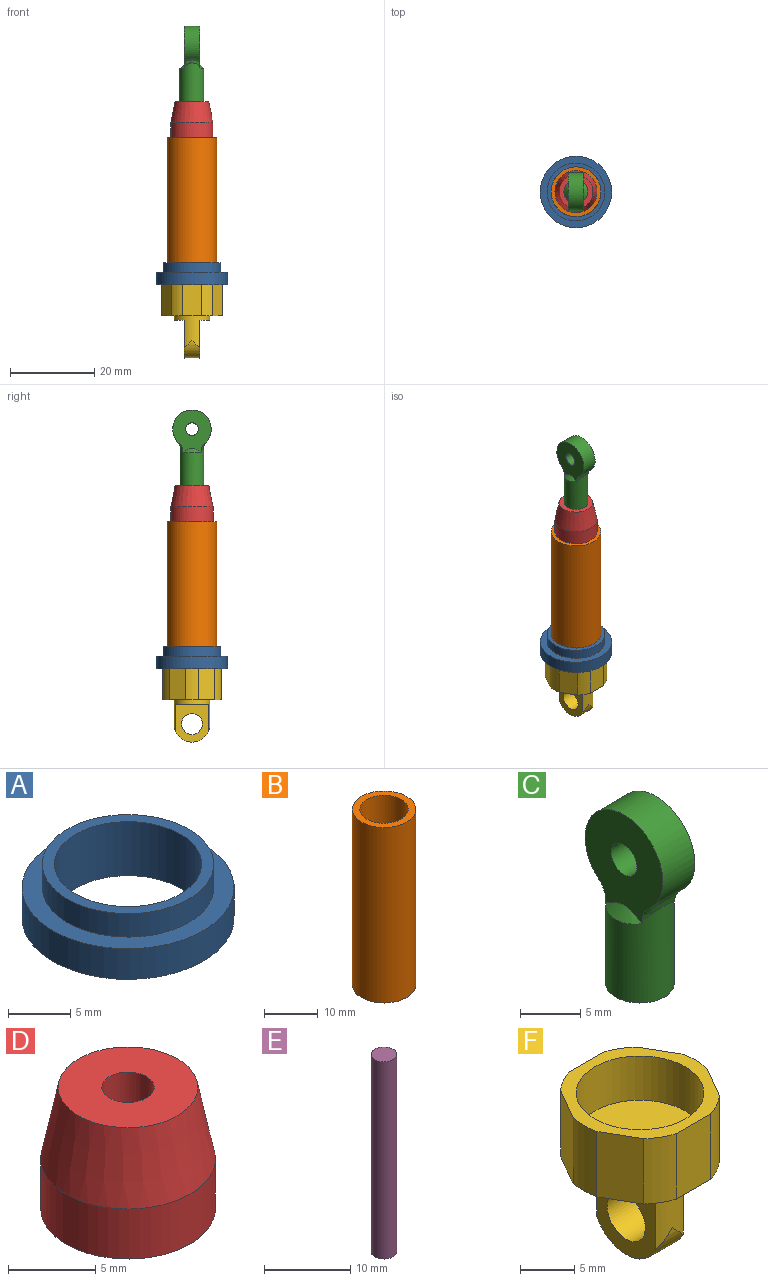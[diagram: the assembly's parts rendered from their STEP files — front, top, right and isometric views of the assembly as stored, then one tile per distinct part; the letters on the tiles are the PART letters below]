
ASSEMBLY  parts=6 mates=11
PART A: 6 faces, bbox 17x17x5.3 mm
  f0: cylinder r=8.5mm len=17mm, axis (0,0,-1), area 160.2mm2, adj f2,f3
  f1: cylinder r=5.9mm len=11.8mm, axis (0,0,-1), area 196.5mm2, adj f3,f5
  f2: plane 17x17mm, normal (0,0,1), area 78.5mm2, adj f0,f4
  f3: plane 17x17mm, normal (0,0,-1), area 117.6mm2, adj f0,f1
  f4: cylinder r=6.88mm len=13.75mm, axis (0,0,-1), area 99.4mm2, adj f2,f5
  f5: plane 13.75x13.75mm, normal (0,0,1), area 39.1mm2, adj f1,f4
PART B: 4 faces, bbox 11.8x11.8x40 mm
  f0: cylinder r=4.5mm len=40mm, axis (0,0,-1), area 1131mm2, adj f2,f3
  f1: cylinder r=5.9mm len=40mm, axis (0,0,-1), area 1482.8mm2, adj f2,f3
  f2: plane 11.8x11.8mm, normal (0,0,1), area 45.7mm2, adj f0,f1
  f3: plane 11.8x11.8mm, normal (0,0,-1), area 45.7mm2, adj f0,f1
PART C: 10 faces, bbox 9.6x11.9x20.8 mm
  f0: cylinder r=2.85mm len=9.25mm, axis (0,0,-1), area 150.1mm2, adj f1,f2,f4,f5,f7,f8,f9
  f1: bspline ~4.29x0.97mm, area 0mm2, adj f0,f8
  f2: bspline ~6.67x2.28mm, area 5.5mm2, adj f0,f3,f5,f8
  f3: cylinder r=4.55mm len=9.1mm, axis (-1,0,0), area 80.9mm2, adj f2,f5,f7,f8
  f4: bspline ~4.29x0.97mm, area 0mm2, adj f0,f5
  f5: plane 12.72x11.86mm, normal (1,0,0), area 60.7mm2, adj f0,f2,f3,f4,f6,f7
  f6: cylinder r=1.5mm len=3.75mm, axis (1,0,0), area 35.3mm2, adj f5,f8
  f7: bspline ~6.67x2.28mm, area 5.5mm2, adj f0,f3,f5,f8
  f8: plane 12.73x11.86mm, normal (-1,0,0), area 60.7mm2, adj f0,f1,f2,f3,f6,f7
  f9: plane 5.7x5.7mm, normal (0,0,-1), area 25.5mm2, adj f0
PART D: 5 faces, bbox 10x10x8.5 mm
  f0: cylinder r=5mm len=10mm, axis (0,0,-1), area 110mm2, adj f1,f3
  f1: plane 10x10mm, normal (0,0,-1), area 71.5mm2, adj f0,f4
  f2: plane 8x8mm, normal (0,0,1), area 43.2mm2, adj f3,f4
  f3: cone r=4mm half-angle=11.3deg, axis (0,0,-1), area 144.2mm2, adj f0,f2
  f4: cylinder r=1.5mm len=8.5mm, axis (0,0,1), area 80.1mm2, adj f1,f2
PART E: 3 faces, bbox 3x3x28 mm
  f0: cylinder r=1.5mm len=28mm, axis (0,0,-1), area 263.9mm2, adj f1,f2
  f1: plane 3x3mm, normal (0,0,1), area 7.1mm2, adj f0
  f2: plane 3x3mm, normal (0,0,-1), area 7.1mm2, adj f0
PART F: 23 faces, bbox 14.7x14x17.4 mm
  f0: plane 9x7.69mm, normal (1,0,0), area 44.3mm2, adj f18,f19,f21,f22
  f1: plane 9x7.69mm, normal (-1,0,0), area 44.3mm2, adj f18,f19,f20,f21
  f2: plane 14.7x14mm, normal (0,0,-1), area 106.7mm2, adj f3,f4,f5,f6,f7,f8,f9,f10
  f3: plane 7.4x4.48mm, normal (0,-1,0), area 33.2mm2, adj f2,f4,f14,f15
  f4: cylinder r=7.35mm len=7.4mm, axis (0,0,-1), area 23.3mm2, adj f2,f3,f5,f15
  f5: plane 7.4x3.88mm, normal (0.87,-0.5,0), area 33.2mm2, adj f2,f4,f6,f15
  f6: cylinder r=7.35mm len=7.4mm, axis (0,0,-1), area 23.3mm2, adj f2,f5,f7,f15
  f7: plane 7.4x3.88mm, normal (0.87,0.5,0), area 33.2mm2, adj f2,f6,f8,f15
  f8: cylinder r=7.35mm len=7.4mm, axis (0,0,-1), area 23.3mm2, adj f2,f7,f9,f15
  f9: plane 7.4x4.48mm, normal (0,1,0), area 33.2mm2, adj f2,f8,f10,f15
  f10: cylinder r=7.35mm len=7.4mm, axis (0,0,-1), area 23.3mm2, adj f2,f9,f11,f15
  f11: plane 7.4x3.88mm, normal (-0.87,0.5,0), area 33.2mm2, adj f2,f10,f12,f15
  f12: cylinder r=7.35mm len=7.4mm, axis (0,0,-1), area 23.3mm2, adj f2,f11,f13,f15
  f13: plane 7.4x3.88mm, normal (-0.87,-0.5,0), area 33.2mm2, adj f2,f12,f14,f15
  f14: cylinder r=7.35mm len=7.4mm, axis (0,0,-1), area 23.3mm2, adj f2,f3,f13,f15
  f15: plane 14.7x14mm, normal (0,0,1), area 54.1mm2, adj f3,f4,f5,f6,f7,f8,f9,f10
  f16: cylinder r=5.9mm len=11.8mm, axis (0,0,1), area 185.4mm2, adj f15,f17
  f17: plane 11.8x11.8mm, normal (0,0,1), area 109.4mm2, adj f16
  f18: cylinder r=4.25mm len=8.5mm, axis (-1,0,0), area 41.7mm2, adj f0,f1,f21
  f19: cylinder r=2.5mm len=5mm, axis (-1,0,0), area 56.9mm2, adj f0,f1
  f20: plane 7.69x2.44mm, normal (0,0,-1), area 13.4mm2, adj f1,f21
  f21: cylinder r=4.25mm len=8.5mm, axis (0,0,1), area 69.2mm2, adj f0,f1,f2,f18,f20,f22
  f22: plane 7.69x2.44mm, normal (0,0,-1), area 13.4mm2, adj f0,f21
PLACE A t=(-0.08,0,-3.68)mm
PLACE B rot(axis=(0,0,-1),90deg) t=(-0.08,0,-3.68)mm
PLACE C rot(axis=(0,0,-1),180deg) t=(-0.08,0,-31.68)mm
PLACE D rot(axis=(0,0,-1),180deg) t=(-0.08,0,-3.68)mm
PLACE E t=(-0.08,0,-31.68)mm
PLACE F t=(-0.08,0,-3.68)mm fixed
MATE cylindrical D.f0 <-> B.f1  axis (0,0,-1) through (-0.08,0,38.72)mm
MATE slider E.f0 <-> D.f3  axis (0,0,-1) through (-0.08,0,19.22)mm
MATE cylindrical E.f0 <-> D.f4  axis (0,0,-1) through (-0.08,0,19.22)mm
MATE planar C.f0 <-> E.f0  axis (0,0,-1) through (-0.08,0,47.22)mm
MATE parallel C.f5 <-> F.f1  axis (-1,0,0) through (-1.95,0,60.47)mm
MATE planar D.f0 <-> B.f1  axis (0,0,-1) through (-0.08,0,38.72)mm
MATE planar F.f16 <-> B.f1  axis (0,0,1) through (-0.08,0,-1.28)mm
MATE cylindrical E.f0 <-> C.f0  axis (0,0,1) through (-0.08,0,47.22)mm
MATE cylindrical F.f16 <-> B.f1  axis (0,0,1) through (-0.08,0,1.22)mm
MATE cylindrical A.f1 <-> B.f1  axis (0,0,-1) through (-0.08,0,9.02)mm
MATE planar A.f0 <-> F.f8  axis (0,0,-1) through (-0.08,0,3.72)mm
